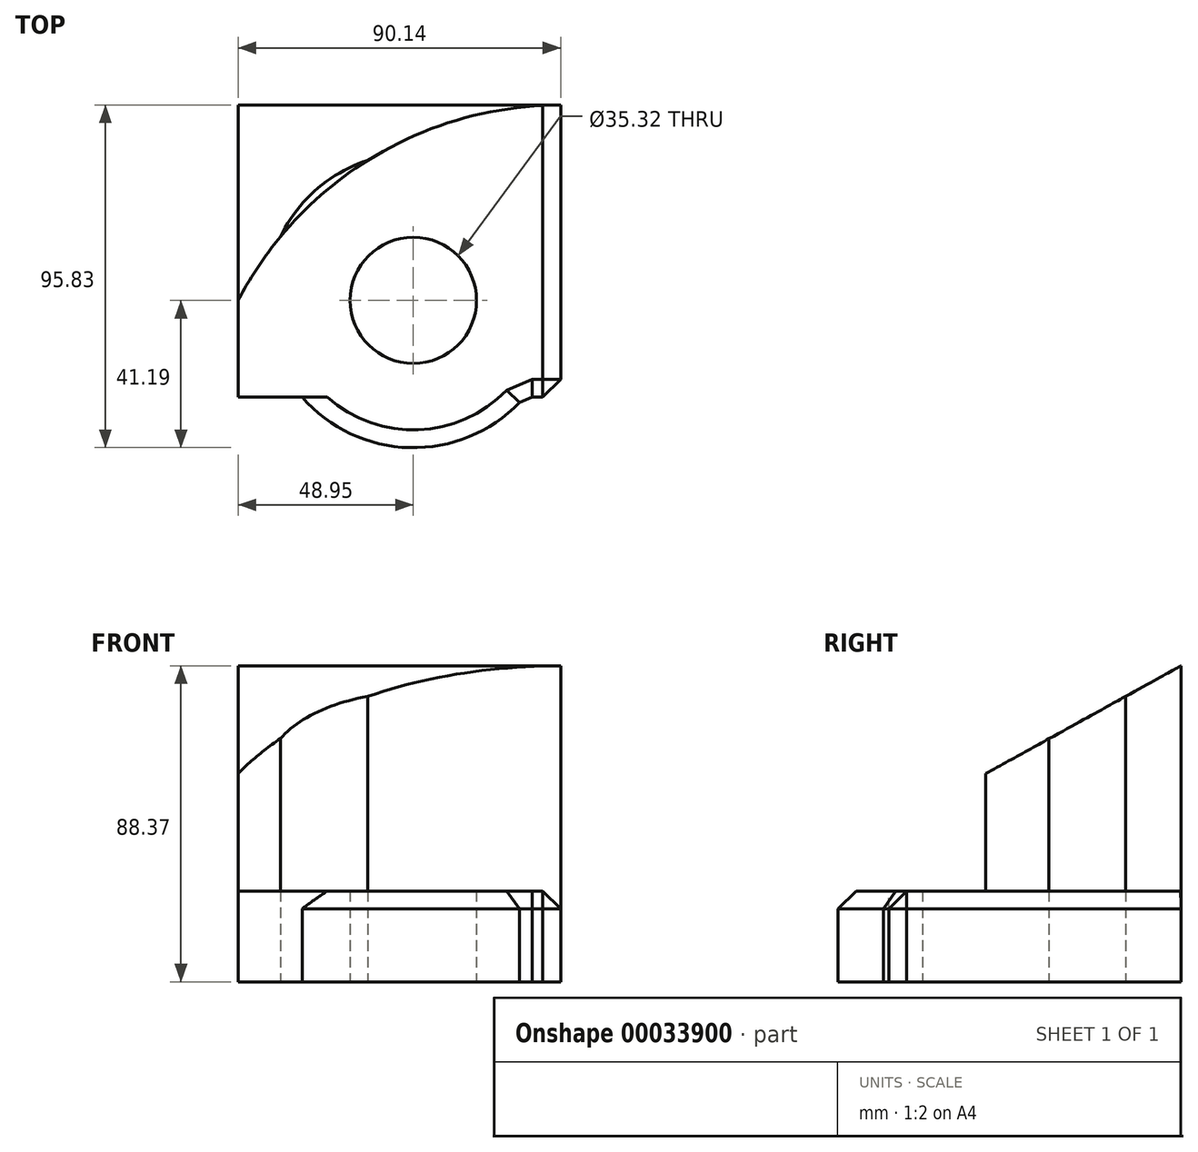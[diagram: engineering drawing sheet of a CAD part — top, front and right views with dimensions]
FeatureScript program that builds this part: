
annotation { "Feature Type Name" : "Feature", "Feature Type Description" : "" }
export const myFeature = defineFeature(function(context is Context, id is Id, definition is map)
    precondition{}
    {
        {
            var Q0;
            Q0=qCreatedBy(makeId("Top.planeOp"),FACE);
            var sketch = newSketch(context, id + "F0", { "sketchPlane" : qUnion([Q0])});
            skLineSegment(sketch, "E0.bottom", {"start": v(-48.95, -27.04) * mm, "end": v(41.2, -27.04) * mm});
            skLineSegment(sketch, "E0.top", {"start": v(-48.95, 54.64) * mm, "end": v(41.2, 54.64) * mm});
            skLineSegment(sketch, "E0.left", {"start": v(-48.95, -27.04) * mm, "end": v(-48.95, 54.64) * mm});
            skLineSegment(sketch, "E0.right", {"start": v(41.2, -27.04) * mm, "end": v(41.2, 54.64) * mm});
            skArc(sketch, "E1", {"start": v(41.2, 54.64) * mm, "mid": v(-11.51, 39.92) * mm, "end": v(-48.95, 0) * mm});
            skCircle(sketch, "E2", {"center": v(0, 0) * mm, "radius": 41.2 * mm});
            skCircle(sketch, "E3", {"center": v(0, 0) * mm, "radius": 17.66 * mm});
            skSolve(sketch);
        }
        {
            var Q0;
            {var subQ6=sQuery(id+"F0.wireOp",EDGE,"E0.top");Q0=makeQuery(id+"F0.imprint","IMPRINT",FACE,{"disambiguationData":[TD([[makeQuery(id+"F0.imprint","IMPRINT",EDGE,{"derivedFrom":subQ6}),-1.0]])]});}
            extrude(context, id + "F1", {"entities" : qUnion([Q0]), "depth" : 127 * mm});
        }
        {
            var Q0;
            Q0 = qSketchRegion(id + "F0", true);
            extrude(context, id + "F2", {"entities" : qUnion([Q0]), "operationType" : NewBodyOperationType.ADD, "depth" : 25.4 * mm});
        }
        {
            var Q0;
            Q0=makeQuery(id+"F2.opExtrude","SWEPT_EDGE",EDGE,{"disambiguationData":[OSD([sQuery(id+"F0.wireOp",EDGE,"E0.bottom"),sQuery(id+"F0.wireOp",EDGE,"E0.right")])]});
            var Q1;
            {var subQ0=sQuery(id+"F0.wireOp",EDGE,"E0.bottom");var subQ1=sQuery(id+"F0.wireOp",EDGE,"E2");Q1=makeQuery(id+"F2.opExtrude","SWEPT_EDGE",EDGE,{"disambiguationData":[OSD([subQ0,subQ1]),TDD([makeQuery(id+"F0.imprint","INTERSECT",VERTEX,{"disambiguationData":[OD(1.0)],"derivedFrom":[subQ0,subQ1]})])]});}
            var Q2;
            {var subQ0=sQuery(id+"F0.wireOp",EDGE,"E2");var subQ1=sQuery(id+"F0.wireOp",EDGE,"E0.bottom");Q2=makeQuery(id+"F2.opExtrude","CAP_EDGE",EDGE,{"disambiguationData":[OSD([subQ0]),TDD([makeQuery(id+"F0.imprint","IMPRINT",EDGE,{"disambiguationData":[TD([[makeQuery(id+"F0.imprint","INTERSECT",VERTEX,{"disambiguationData":[OD(0.0)],"derivedFrom":[subQ1,subQ0]}),-1.0]])],"derivedFrom":subQ0})])],"isStart":false});}
            var Q3;
            Q3=makeQuery(id+"F2.opExtrude","CAP_EDGE",EDGE,{"disambiguationData":[OSD([sQuery(id+"F0.wireOp",EDGE,"E0.right")])],"isStart":false});
            chamfer(context, id + "F3", {"entities" : qUnion([Q0, Q1, Q2, Q3]), "width" : 5 * mm, "tangentPropagation" : true});
        }
        {
            var Q0;
            {var subQ0=sQuery(id+"F0.wireOp",EDGE,"E0.left");Q0=makeQuery(id+"F2.boolean.opBoolean","MERGE",FACE,{"derivedFrom":[makeQuery(id+"F1.opExtrude","SWEPT_FACE",FACE,{"disambiguationData":[OSD([subQ0])]}),makeQuery(id+"F2.opExtrude","SWEPT_FACE",FACE,{"disambiguationData":[OSD([subQ0])]})]});}
            var sketch = newSketch(context, id + "F4", { "sketchPlane" : qUnion([Q0])});
            skLineSegment(sketch, "E4", {"start": v(0, 58.18) * mm, "end": v(-54.64, 88.37) * mm});
            skSolve(sketch);
        }
        {
            var Q0;
            {var subQ2=sQuery(id+"F4.wireOp",EDGE,"E4");Q0=makeQuery(id+"F4.imprint","IMPRINT",FACE,{"disambiguationData":[TD([[makeQuery(id+"F4.imprint","IMPRINT",EDGE,{"derivedFrom":subQ2}),-1.0]])]});}
            extrude(context, id + "F5", {"entities" : qUnion([Q0]), "operationType" : NewBodyOperationType.REMOVE, "oppositeDirection" : true, "depth" : 171.05 * mm});
        }
    });
